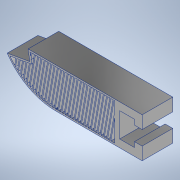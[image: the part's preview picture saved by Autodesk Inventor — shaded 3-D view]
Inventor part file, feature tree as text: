
AUTODESK INVENTOR PART (.ipt)
format: ipt  version: 2022 (Build 260153000, 153)  size: 487,936 bytes
history: native  units: mm
features: extrude x6, sketch x5, fillet x1, shell x1, projected_geometry x1
ambient origin geometry x8: Origin, YZ Plane, XZ Plane, XY Plane, X Axis, Y Axis, Z Axis, Center Point
bodies: Body1 (feature_tree)
feature tree (14):
  extrude  "Extrusion2"  Depth=5.8mm
  extrude  "Extrusion5"  Depth=12.0mm TaperAngle=0.0deg
  fillet  "Fillet2"  Radius=45.0mm
  shell  "Shell1"  Thickness=15.6mm
  extrude  "Extrusion7"  TaperAngle=0.0deg  [1 undecoded]
  extrude  "Extrusion8"  Depth=9.6mm
  extrude  "Extrusion9"  Depth=12.0mm
  extrude  "Extrusion10"  Depth=15.6mm
  sketch  "Sketch8"  dims[d41=5.8mm d48=44.0mm]
  sketch  "Sketch13"  dims[d50=3.0mm d56=12.0mm d57=0.0mm d63=45.0mm d67=15.6mm d71=0.0mm]
  sketch  "Sketch14"  dims[d80=17.453293mm d82=0.0mm d83=0.0mm]
  projected_geometry  "Projected Loop1"
  sketch  "Sketch15"  dims[d87=5.6mm d88=9.6mm]
  sketch  "Sketch16"  dims[d95=4.0mm d96=9.0mm d97=15.6mm d98=23.0mm d99=0.62mm d100=12.0mm d101=0.0mm d102=10.747401mm d103=12.0mm d104=0.0mm d105=0.38mm d107=0.38mm d1=0.38mm d108=0.38mm d109=0.38mm d110=0.38mm d111=0.38mm d112=0.38mm d113=0.38mm d127=12.0mm d128=0.0mm d129=0.38mm d131=0.38mm d132=0.38mm d133=0.38mm d134=0.38mm d135=0.38mm d136=0.38mm d137=0.38mm d138=0.38mm d139=0.38mm d151=0.38mm d157=0.38mm d161=0.38mm d163=0.38mm d168=0.89mm d169=0.38mm d170=0.89mm d171=0.89mm d172=0.38mm d173=0.89mm d174=0.89mm d175=0.38mm d176=0.89mm d178=0.38mm d179=0.89mm d182=0.89mm d184=0.89mm d185=17.453293mm d186=17.453293mm d187=17.453293mm d188=0.89mm d189=0.89mm d190=0.89mm d191=0.89mm d192=0.89mm d193=0.89mm d194=0.89mm d195=0.89mm d196=0.89mm d197=0.89mm d198=0.89mm d200=0.38mm d201=17.453293mm d202=0.89mm d203=0.89mm d204=0.89mm d205=0.89mm d206=0.89mm d207=0.89mm d209=0.89mm d210=0.38mm d211=0.38mm d212=0.89mm d213=0.89mm d214=0.38mm d215=0.38mm d216=0.38mm d217=0.89mm d218=0.89mm d219=12.0mm d220=0.0mm]
note: 1 required parameter value undecoded (feature->parameter linkage not recoverable at this tier; creation-order binding heuristic only, values carry confidence <= 0.55)
